# Revit family: FU_Inspec_Add_Move_4-4
name_source: partatom
category: Furniture
units: mm (PartAtom-declared; Revit-internal decimal feet)

## family parameters
Always vertical = Yes
Cut with Voids When Loaded = No
OmniClass Number = 23.40.20.00
OmniClass Title = General Furniture and Specialties
Room Calculation Point = No
Shared = No
Work Plane-Based = No

## types (5) — shared parameters
Assembly Code = E2020
Depth = 560 mm  [stored 1.83727 ft]
Height = 490 mm  [stored 1.60761 ft]
Keynote = 46.B
Manufacturer = Inspec
URL = https://inspecfurniture.com
Weight = 4.0
Width = 480 mm  [stored 1.5748 ft]
zero-valued in all types: Default Elevation

## per-type parameters (varying)
| type | Back Material | Backrest | Description | Frame Material | Model | Seat Material |
| add move stool 4.4 | Fabric - Rust Red Woven | No | Counter stool with seat of upholstered molded wood and polyurethane foam, on a powder coated or chromium plated steel tubular frame. With casters and chrome footrest | Metal - Chrome - Polished | add move stool 4.4 | Fabric - Rust Red Woven |
| add move stool 4.3 | Plastic - Black | No | Counter stool with seat of molded wood and polyurethane foam, on a powder coated or chromium plated steel tubular frame. With casters and chrome footrest | Metal - Black - Matte | add move stool 4.3 | Plastic - Black |
| Add Move Stool 3.2 | Plastic - Black | Yes | Barstool with seat of upholstered molded wood and polyurethane foam and polyurethane backrest, on a powder coated or chromium plated steel tubular frame. With casters and chrome footrest. | Metal - Black - Matte | add move stool 3.2 | Fabric - Rust Red Woven |
| add move stool 3.3 | Fabric - Rust Red Woven | Yes | Barstool with seat and back of upholstered molded wood and polyurethane foam, on a powder coated or chromium plated steel tubular frame. With casters and chrome footrest | Metal - Chrome - Polished | add move stool 3.3 | Fabric - Rust Red Woven |
| Add Move Stool 3.1 | Plastic - Black | Yes | Barstool with seat and back of molded wood and polyurethane foam, on a powder coated or chromium plated steel tubular frame. With casters and chrome footrest | Metal - Black - Matte | add move stool 3.1 | Plastic - Black |

note: [stored X ft] marks values corroborated as IEEE doubles in the binary element streams (Revit-internal decimal feet)

## geometry (parser evidence)
native form markers: Blend x4, Sweep x2
no freeform markers — native parametric forms only
